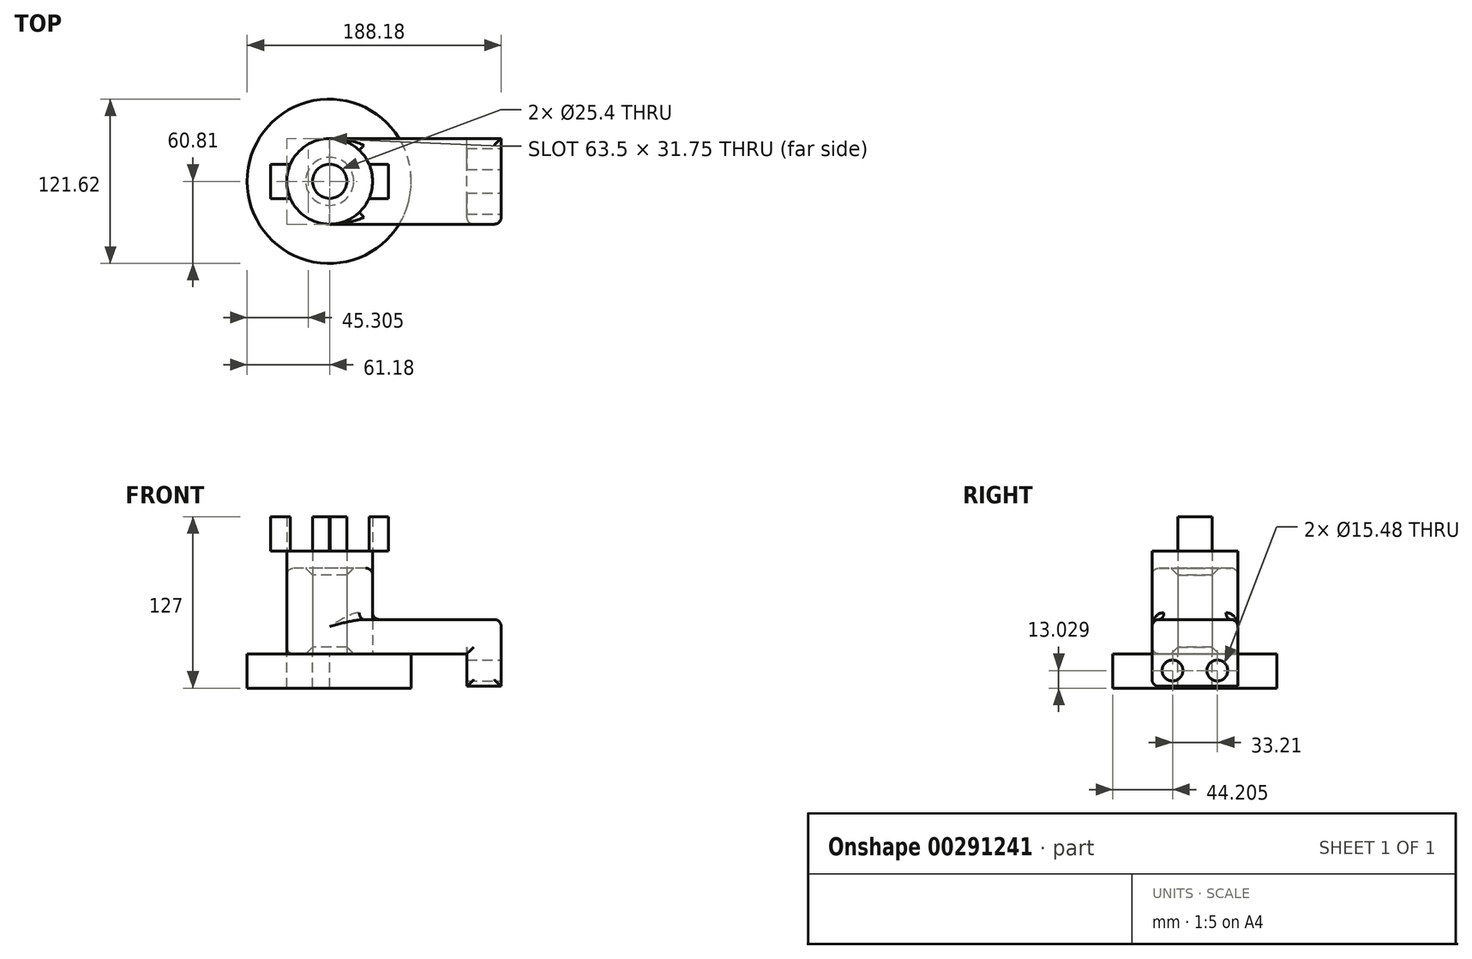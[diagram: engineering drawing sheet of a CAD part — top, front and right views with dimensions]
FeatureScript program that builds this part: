
annotation { "Feature Type Name" : "Feature", "Feature Type Description" : "" }
export const myFeature = defineFeature(function(context is Context, id is Id, definition is map)
    precondition{}
    {
        {
            var Q0;
            Q0=qCreatedBy(makeId("Top.planeOp"),FACE);
            var sketch = newSketch(context, id + "F0", { "sketchPlane" : qUnion([Q0])});
            skLineSegment(sketch, "E0.bottom", {"start": v(63.5, -31.75) * mm, "end": v(-63.5, -31.75) * mm});
            skLineSegment(sketch, "E0.top", {"start": v(63.5, 31.75) * mm, "end": v(-63.5, 31.75) * mm});
            skLineSegment(sketch, "E0.left", {"start": v(63.5, -31.75) * mm, "end": v(63.5, 31.75) * mm});
            skLineSegment(sketch, "E0.right", {"start": v(-63.5, -31.75) * mm, "end": v(-63.5, 31.75) * mm});
            skPoint(sketch, "E0.middle", {"position": v(0, 0) * mm});
            skCircle(sketch, "E1", {"center": v(-63.5, 0) * mm, "radius": 31.75 * mm});
            skCircle(sketch, "E2", {"center": v(-63.5, 0) * mm, "radius": 12.7 * mm});
            skSolve(sketch);
        }
        {
            var Q0;
            Q0 = qSketchRegion(id + "F0", true);
            extrude(context, id + "F1", {"entities" : qUnion([Q0]), "depth" : 25.4 * mm});
        }
        {
            var Q0;
            {var subQ1=sQuery(id+"F0.wireOp",EDGE,"E0.right");var subQ3=sQuery(id+"F0.wireOp",EDGE,"E2");var subQ4=makeQuery(id+"F0.imprint","INTERSECT",VERTEX,{"disambiguationData":[OD(0.0)],"derivedFrom":[subQ1,subQ3]});Q0=makeQuery(id+"F0.imprint","IMPRINT",FACE,{"disambiguationData":[TD([[makeQuery(id+"F0.imprint","IMPRINT",EDGE,{"disambiguationData":[TD([[subQ4,1.0]])],"derivedFrom":subQ3}),-1.0]])]});}
            var Q1;
            {var subQ1=sQuery(id+"F0.wireOp",EDGE,"E0.right");var subQ3=sQuery(id+"F0.wireOp",EDGE,"E2");var subQ4=makeQuery(id+"F0.imprint","INTERSECT",VERTEX,{"disambiguationData":[OD(0.0)],"derivedFrom":[subQ1,subQ3]});Q1=makeQuery(id+"F0.imprint","IMPRINT",FACE,{"disambiguationData":[TD([[makeQuery(id+"F0.imprint","IMPRINT",EDGE,{"disambiguationData":[TD([[subQ4,-1.0]])],"derivedFrom":subQ3}),-1.0]])]});}
            extrude(context, id + "F2", {"entities" : qUnion([Q0, Q1]), "operationType" : NewBodyOperationType.ADD, "depth" : 63.5 * mm});
        }
        {
            var Q0;
            Q0=makeQuery(id+"F1.opExtrude","SWEPT_FACE",FACE,{"disambiguationData":[OSD([sQuery(id+"F0.wireOp",EDGE,"E0.left")])]});
            var sketch = newSketch(context, id + "F3", { "sketchPlane" : qUnion([Q0])});
            skLineSegment(sketch, "E3.bottom", {"start": v(-31.75, 25.4) * mm, "end": v(31.75, 25.4) * mm});
            skLineSegment(sketch, "E3.top", {"start": v(-31.75, -24.1) * mm, "end": v(31.75, -24.1) * mm});
            skLineSegment(sketch, "E3.left", {"start": v(-31.75, 25.4) * mm, "end": v(-31.75, -24.1) * mm});
            skLineSegment(sketch, "E3.right", {"start": v(31.75, 25.4) * mm, "end": v(31.75, -24.1) * mm});
            skLineSegment(sketch, "E4", {"start": v(0, 0) * mm, "end": v(0, -24.1) * mm, "construction": true});
            skCircle(sketch, "E5", {"center": v(-16.6, -12.37) * mm, "radius": 7.74 * mm});
            skCircle(sketch, "E6.MirrorC", {"center": v(16.6, -12.37) * mm, "radius": 7.74 * mm});
            skSolve(sketch);
        }
        {
            var Q0;
            Q0 = qSketchRegion(id + "F3", true);
            extrude(context, id + "F4", {"entities" : qUnion([Q0]), "operationType" : NewBodyOperationType.ADD, "oppositeDirection" : true, "depth" : 25.4 * mm});
        }
        {
            var Q0;
            Q0=makeQuery(id+"F1.opExtrude","CAP_FACE",FACE,{"disambiguationData":[OSD([sQuery(id+"F0.wireOp",EDGE,"E0.bottom"),sQuery(id+"F0.wireOp",EDGE,"E0.top"),sQuery(id+"F0.wireOp",EDGE,"E0.left"),sQuery(id+"F0.wireOp",EDGE,"E1"),sQuery(id+"F0.wireOp",EDGE,"E2")])],"isStart":false});
            var Q1;
            {var subQ0=sQuery(id+"F0.wireOp",EDGE,"E1");Q1=makeQuery(id+"F2.boolean.opBoolean","MERGE",FACE,{"derivedFrom":[makeQuery(id+"F1.opExtrude","SWEPT_FACE",FACE,{"disambiguationData":[OSD([subQ0])]}),makeQuery(id+"F2.opExtrude","SWEPT_FACE",FACE,{"disambiguationData":[OSD([subQ0])]})]});}
            var Q2;
            Q2=makeQuery(id+"F4.boolean.opBoolean","MERGE",FACE,{"derivedFrom":[makeQuery(id+"F1.opExtrude","SWEPT_FACE",FACE,{"disambiguationData":[OSD([sQuery(id+"F0.wireOp",EDGE,"E0.bottom")])]}),makeQuery(id+"F4.opExtrude","SWEPT_FACE",FACE,{"disambiguationData":[OSD([sQuery(id+"F3.wireOp",EDGE,"E3.left")])]})]});
            fillet(context, id + "F5", {"entities" : qUnion([Q0, Q1, Q2]), "radius" : 5.08 * mm, "tangentPropagation" : true, "allowEdgeOverflow" : false});
        }
        {
            var Q0;
            {var subQ0=sQuery(id+"F0.wireOp",EDGE,"E2");Q0=makeQuery(id+"F2.boolean.opBoolean","MERGE",FACE,{"derivedFrom":[makeQuery(id+"F1.opExtrude","SWEPT_FACE",FACE,{"disambiguationData":[OSD([subQ0])]}),makeQuery(id+"F2.opExtrude","SWEPT_FACE",FACE,{"disambiguationData":[OSD([subQ0])]})]});}
            var Q1;
            Q1=makeQuery(id+"F2.opExtrude","CAP_FACE",FACE,{"disambiguationData":[OSD([sQuery(id+"F0.wireOp",EDGE,"E1"),sQuery(id+"F0.wireOp",EDGE,"E2")])],"isStart":false});
            chamfer(context, id + "F6", {"entities" : qUnion([Q0, Q1]), "width" : 5.08 * mm, "tangentPropagation" : true});
        }
        {
            var Q0;
            {var subQ0=sQuery(id+"F0.wireOp",EDGE,"E2");var subQ1=sQuery(id+"F0.wireOp",EDGE,"E0.right");var subQ2=makeQuery(id+"F0.imprint","INTERSECT",VERTEX,{"disambiguationData":[OD(0.0)],"derivedFrom":[subQ1,subQ0]});Q0=makeQuery(id+"F0.imprint","IMPRINT",FACE,{"disambiguationData":[TD([[makeQuery(id+"F0.imprint","IMPRINT",EDGE,{"disambiguationData":[TD([[subQ2,-1.0]])],"derivedFrom":subQ1}),1.0]])]});}
            var Q1;
            {var subQ0=sQuery(id+"F0.wireOp",EDGE,"E2");var subQ1=sQuery(id+"F0.wireOp",EDGE,"E0.right");var subQ2=makeQuery(id+"F0.imprint","INTERSECT",VERTEX,{"disambiguationData":[OD(0.0)],"derivedFrom":[subQ1,subQ0]});Q1=makeQuery(id+"F0.imprint","IMPRINT",FACE,{"disambiguationData":[TD([[makeQuery(id+"F0.imprint","IMPRINT",EDGE,{"disambiguationData":[TD([[subQ2,-1.0]])],"derivedFrom":subQ1}),-1.0]])]});}
            extrude(context, id + "F7", {"entities" : qUnion([Q0, Q1]), "depth" : 76.2 * mm});
        }
        {
            var Q0;
            Q0=makeQuery(id+"F7.opExtrude","CAP_FACE",FACE,{"disambiguationData":[OSD([sQuery(id+"F0.wireOp",EDGE,"E2")])],"isStart":false});
            var sketch = newSketch(context, id + "F8", { "sketchPlane" : qUnion([Q0])});
            skLineSegment(sketch, "E7.bottom", {"start": v(-19.85, -12.7) * mm, "end": v(-107.15, -12.7) * mm});
            skLineSegment(sketch, "E7.top", {"start": v(-19.85, 12.7) * mm, "end": v(-107.15, 12.7) * mm});
            skLineSegment(sketch, "E7.left", {"start": v(-19.85, -12.7) * mm, "end": v(-19.85, 12.7) * mm});
            skLineSegment(sketch, "E7.right", {"start": v(-107.15, -12.7) * mm, "end": v(-107.15, 12.7) * mm});
            skPoint(sketch, "E7.middle", {"position": v(-63.5, 0) * mm});
            skSolve(sketch);
        }
        {
            var Q0;
            {var subQ0=sQuery(id+"F8.wireOp",EDGE,"E7.left");Q0=makeQuery(id+"F8.imprint","IMPRINT",FACE,{"disambiguationData":[TD([[makeQuery(id+"F8.imprint","IMPRINT",EDGE,{"derivedFrom":subQ0}),1.0]])]});}
            var Q1;
            {var subQ0=sQuery(id+"F8.wireOp",EDGE,"E7.right");Q1=makeQuery(id+"F8.imprint","IMPRINT",FACE,{"disambiguationData":[TD([[makeQuery(id+"F8.imprint","IMPRINT",EDGE,{"derivedFrom":subQ0}),-1.0]])]});}
            var Q2;
            {var subQ0=sQuery(id+"F8.wireOp",EDGE,"E7.bottom");var subQ1=makeQuery(id+"F7.opExtrude","CAP_EDGE",EDGE,{"disambiguationData":[OSD([sQuery(id+"F0.wireOp",EDGE,"E2")])],"isStart":false});var subQ2=makeQuery(id+"F8.imprint","INTERSECT",VERTEX,{"disambiguationData":[OD(0.0)],"derivedFrom":[subQ1,subQ0]});Q2=makeQuery(id+"F8.imprint","IMPRINT",FACE,{"disambiguationData":[TD([[makeQuery(id+"F8.imprint","IMPRINT",EDGE,{"disambiguationData":[TD([[subQ2,-1.0]])],"derivedFrom":subQ0}),-1.0]])]});}
            extrude(context, id + "F9", {"entities" : qUnion([Q0, Q1, Q2]), "operationType" : NewBodyOperationType.ADD, "depth" : 25.4 * mm});
        }
        {
            var Q0;
            {var subQ0=sQuery(id+"F0.wireOp",EDGE,"E2");var subQ1=sQuery(id+"F0.wireOp",EDGE,"E0.right");var subQ2=makeQuery(id+"F0.imprint","INTERSECT",VERTEX,{"disambiguationData":[OD(0.0)],"derivedFrom":[subQ1,subQ0]});Q0=makeQuery(id+"F0.imprint","IMPRINT",FACE,{"disambiguationData":[TD([[makeQuery(id+"F0.imprint","IMPRINT",EDGE,{"disambiguationData":[TD([[subQ2,-1.0]])],"derivedFrom":subQ1}),1.0]])]});}
            var sketch = newSketch(context, id + "F10", { "sketchPlane" : qUnion([Q0])});
            skCircle(sketch, "E8", {"center": v(-63.87, 0) * mm, "radius": 60.8 * mm});
            skSolve(sketch);
        }
        {
            var Q0;
            Q0=makeQuery(id+"F10.imprint","IMPRINT",FACE,{"disambiguationData":[TD([[makeQuery(id+"F10.imprint","IMPRINT",EDGE,{"derivedFrom":sQuery(id+"F10.wireOp",EDGE,"E8")}),1.0]])]});
            extrude(context, id + "F11", {"entities" : qUnion([Q0]), "oppositeDirection" : true, "depth" : 25.4 * mm});
        }
    });
